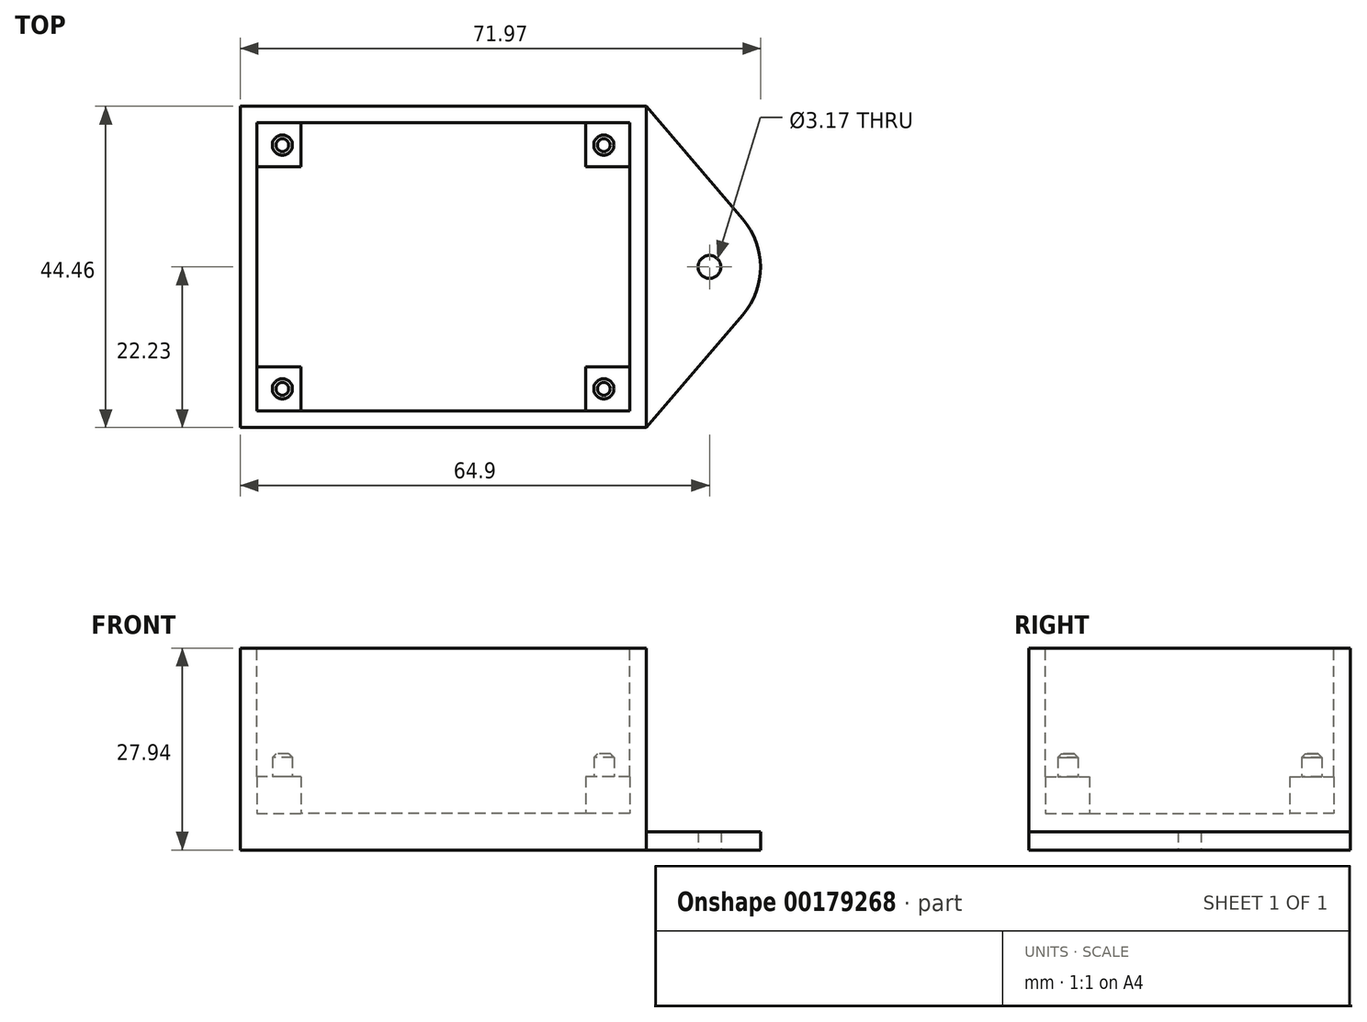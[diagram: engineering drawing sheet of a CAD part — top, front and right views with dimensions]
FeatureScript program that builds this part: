
annotation { "Feature Type Name" : "Feature", "Feature Type Description" : "" }
export const myFeature = defineFeature(function(context is Context, id is Id, definition is map)
    precondition{}
    {
        {
            var Q0;
            Q0=qCreatedBy(makeId("Top.planeOp"),FACE);
            var sketch = newSketch(context, id + "F0", { "sketchPlane" : qUnion([Q0])});
            skLineSegment(sketch, "E0.bottom", {"start": v(28.07, -22.23) * mm, "end": v(-28.07, -22.23) * mm});
            skLineSegment(sketch, "E0.top", {"start": v(28.07, 22.23) * mm, "end": v(-28.07, 22.22) * mm});
            skLineSegment(sketch, "E0.left", {"start": v(28.07, -22.23) * mm, "end": v(28.07, 22.23) * mm});
            skLineSegment(sketch, "E0.right", {"start": v(-28.07, -22.23) * mm, "end": v(-28.07, 22.23) * mm});
            skPoint(sketch, "E0.middle", {"position": v(0, 0) * mm});
            skSolve(sketch);
        }
        {
            var Q0;
            Q0 = qSketchRegion(id + "F0", true);
            extrude(context, id + "F1", {"entities" : qUnion([Q0]), "depth" : 27.94 * mm});
        }
        {
            var Q0;
            Q0=makeQuery(id+"F1.opExtrude","CAP_FACE",FACE,{"disambiguationData":[OSD([sQuery(id+"F0.wireOp",EDGE,"E0.bottom"),sQuery(id+"F0.wireOp",EDGE,"E0.top"),sQuery(id+"F0.wireOp",EDGE,"E0.left"),sQuery(id+"F0.wireOp",EDGE,"E0.right")])],"isStart":false});
            var sketch = newSketch(context, id + "F2", { "sketchPlane" : qUnion([Q0])});
            skLineSegment(sketch, "E1.0", {"start": v(25.78, 19.94) * mm, "end": v(-25.78, 19.94) * mm});
            skLineSegment(sketch, "E1.1", {"start": v(25.78, -19.94) * mm, "end": v(25.78, 19.94) * mm});
            skLineSegment(sketch, "E1.2", {"start": v(25.78, -19.94) * mm, "end": v(-25.78, -19.94) * mm});
            skLineSegment(sketch, "E1.3", {"start": v(-25.78, -19.94) * mm, "end": v(-25.78, 19.94) * mm});
            skSolve(sketch);
        }
        {
            var Q0;
            Q0 = qSketchRegion(id + "F2", true);
            extrude(context, id + "F3", {"entities" : qUnion([Q0]), "operationType" : NewBodyOperationType.REMOVE, "oppositeDirection" : true, "depth" : 22.86 * mm});
        }
        {
            var Q0;
            Q0=makeQuery(id+"F3.boolean.opBoolean","COPY",FACE,{"derivedFrom":makeQuery(id+"F3.opExtrude","CAP_FACE",FACE,{"disambiguationData":[OSD([sQuery(id+"F2.wireOp",EDGE,"E1.0"),sQuery(id+"F2.wireOp",EDGE,"E1.1"),sQuery(id+"F2.wireOp",EDGE,"E1.2"),sQuery(id+"F2.wireOp",EDGE,"E1.3")])],"isStart":false})});
            var sketch = newSketch(context, id + "F4", { "sketchPlane" : qUnion([Q0])});
            skLineSegment(sketch, "E2.bottom", {"start": v(-25.78, 19.94) * mm, "end": v(-19.69, 19.94) * mm});
            skLineSegment(sketch, "E2.top", {"start": v(-25.78, 13.84) * mm, "end": v(-19.69, 13.84) * mm});
            skLineSegment(sketch, "E2.left", {"start": v(-25.78, 19.94) * mm, "end": v(-25.78, 13.84) * mm});
            skLineSegment(sketch, "E2.right", {"start": v(-19.69, 19.94) * mm, "end": v(-19.69, 13.84) * mm});
            skLineSegment(sketch, "E3.MirrorCS", {"start": v(25.78, 19.94) * mm, "end": v(25.78, 13.84) * mm});
            skLineSegment(sketch, "E4.MirrorCS", {"start": v(19.69, 19.94) * mm, "end": v(19.69, 13.84) * mm});
            skLineSegment(sketch, "E5.MirrorCS", {"start": v(25.78, 13.84) * mm, "end": v(19.69, 13.84) * mm});
            skLineSegment(sketch, "E6.MirrorCS", {"start": v(25.78, 19.94) * mm, "end": v(19.69, 19.94) * mm});
            skLineSegment(sketch, "E7.MirrorCS", {"start": v(-25.78, -13.84) * mm, "end": v(-19.69, -13.84) * mm});
            skLineSegment(sketch, "E8.MirrorCS", {"start": v(-25.78, -19.94) * mm, "end": v(-25.78, -13.84) * mm});
            skLineSegment(sketch, "E9.MirrorCS", {"start": v(-19.69, -19.94) * mm, "end": v(-19.69, -13.84) * mm});
            skLineSegment(sketch, "E10.MirrorCS", {"start": v(-25.78, -19.94) * mm, "end": v(-19.69, -19.94) * mm});
            skLineSegment(sketch, "E11.MirrorCS", {"start": v(25.78, -13.84) * mm, "end": v(19.69, -13.84) * mm});
            skLineSegment(sketch, "E12.MirrorCS", {"start": v(19.69, -19.94) * mm, "end": v(19.69, -13.84) * mm});
            skLineSegment(sketch, "E13.MirrorCS", {"start": v(25.78, -19.94) * mm, "end": v(25.78, -13.84) * mm});
            skLineSegment(sketch, "E14.MirrorCS", {"start": v(25.78, -19.94) * mm, "end": v(19.69, -19.94) * mm});
            skSolve(sketch);
        }
        {
            var Q0;
            Q0 = qSketchRegion(id + "F4", true);
            extrude(context, id + "F5", {"entities" : qUnion([Q0]), "operationType" : NewBodyOperationType.ADD, "depth" : 5.08 * mm});
        }
        {
            var Q0;
            Q0=makeQuery(id+"F5.opExtrude","CAP_FACE",FACE,{"disambiguationData":[OSD([sQuery(id+"F4.wireOp",EDGE,"E2.bottom"),sQuery(id+"F4.wireOp",EDGE,"E2.top"),sQuery(id+"F4.wireOp",EDGE,"E2.left"),sQuery(id+"F4.wireOp",EDGE,"E2.right")])],"isStart":false});
            var sketch = newSketch(context, id + "F6", { "sketchPlane" : qUnion([Q0])});
            skLineSegment(sketch, "E15.bottom", {"start": v(22.23, -16.86) * mm, "end": v(-22.23, -16.86) * mm, "construction": true});
            skLineSegment(sketch, "E15.top", {"start": v(22.23, 16.86) * mm, "end": v(-22.23, 16.86) * mm, "construction": true});
            skLineSegment(sketch, "E15.left", {"start": v(22.23, -16.86) * mm, "end": v(22.23, 16.86) * mm, "construction": true});
            skLineSegment(sketch, "E15.right", {"start": v(-22.23, -16.86) * mm, "end": v(-22.23, 16.86) * mm, "construction": true});
            skPoint(sketch, "E15.middle", {"position": v(0, 0) * mm});
            skCircle(sketch, "E16", {"center": v(-22.23, 16.86) * mm, "radius": 1.4 * mm});
            skCircle(sketch, "E17.MirrorC", {"center": v(22.23, 16.86) * mm, "radius": 1.4 * mm});
            skCircle(sketch, "E18.MirrorC", {"center": v(22.23, -16.86) * mm, "radius": 1.4 * mm});
            skCircle(sketch, "E19.MirrorC", {"center": v(-22.23, -16.86) * mm, "radius": 1.4 * mm});
            skSolve(sketch);
        }
        {
            var Q0;
            Q0 = qSketchRegion(id + "F6", true);
            extrude(context, id + "F7", {"entities" : qUnion([Q0]), "operationType" : NewBodyOperationType.ADD, "depth" : 3.17 * mm});
        }
        {
            var Q0;
            Q0=makeQuery(id+"F7.opExtrude","CAP_EDGE",EDGE,{"disambiguationData":[OSD([sQuery(id+"F6.wireOp",EDGE,"E16")])],"isStart":false});
            var Q1;
            Q1=makeQuery(id+"F7.opExtrude","CAP_EDGE",EDGE,{"disambiguationData":[OSD([sQuery(id+"F6.wireOp",EDGE,"E17.MirrorC")])],"isStart":false});
            var Q2;
            Q2=makeQuery(id+"F7.opExtrude","CAP_EDGE",EDGE,{"disambiguationData":[OSD([sQuery(id+"F6.wireOp",EDGE,"E19.MirrorC")])],"isStart":false});
            var Q3;
            Q3=makeQuery(id+"F7.opExtrude","CAP_EDGE",EDGE,{"disambiguationData":[OSD([sQuery(id+"F6.wireOp",EDGE,"E18.MirrorC")])],"isStart":false});
            chamfer(context, id + "F8", {"entities" : qUnion([Q0, Q1, Q2, Q3]), "width" : 0.5 * mm, "tangentPropagation" : true});
        }
        {
            var Q0;
            Q0=makeQuery(id+"F1.opExtrude","CAP_FACE",FACE,{"disambiguationData":[OSD([sQuery(id+"F0.wireOp",EDGE,"E0.bottom"),sQuery(id+"F0.wireOp",EDGE,"E0.top"),sQuery(id+"F0.wireOp",EDGE,"E0.left"),sQuery(id+"F0.wireOp",EDGE,"E0.right")])],"isStart":true});
            var sketch = newSketch(context, id + "F9", { "sketchPlane" : qUnion([Q0])});
            skLineSegment(sketch, "E20", {"start": v(28.07, 22.23) * mm, "end": v(41.45, 6.61) * mm});
            skLineSegment(sketch, "E21", {"start": v(41.45, -6.61) * mm, "end": v(28.07, -22.23) * mm});
            skPoint(sketch, "E22.visualSharp", {"position": v(47.12, 0) * mm});
            skArc(sketch, "E22.filletArc", {"start": v(41.45, -6.61) * mm, "mid": v(43.9, 0) * mm, "end": v(41.45, 6.61) * mm});
            skLineSegment(sketch, "E23", {"start": v(28.07, 22.23) * mm, "end": v(28.07, -22.23) * mm});
            skArc(sketch, "E24.MirrorCS", {"start": v(-41.45, -6.61) * mm, "mid": v(-43.9, 0) * mm, "end": v(-41.45, 6.61) * mm});
            skLineSegment(sketch, "E25.MirrorCS", {"start": v(-41.45, -6.61) * mm, "end": v(-28.07, -22.23) * mm});
            skLineSegment(sketch, "E26.MirrorCS", {"start": v(-28.07, 22.23) * mm, "end": v(-41.45, 6.61) * mm});
            skLineSegment(sketch, "E27.MirrorCS", {"start": v(-28.07, 22.23) * mm, "end": v(-28.07, -22.23) * mm});
            skPoint(sketch, "E28.MirrorP", {"position": v(-47.12, 0) * mm});
            skSolve(sketch);
        }
        {
            var Q0;
            Q0=makeQuery(id+"F9.imprint","IMPRINT",FACE,{"disambiguationData":[TD([[makeQuery(id+"F9.imprint","IMPRINT",EDGE,{"derivedFrom":sQuery(id+"F9.wireOp",EDGE,"E20")}),-1.0]])]});
            var Q1;
            Q1=makeQuery(id+"F9.imprint","IMPRINT",FACE,{"disambiguationData":[TD([[makeQuery(id+"F9.imprint","IMPRINT",EDGE,{"derivedFrom":sQuery(id+"F9.wireOp",EDGE,"E24.MirrorCS")}),-1.0]])]});
            extrude(context, id + "F10", {"entities" : qUnion([Q0, Q1]), "operationType" : NewBodyOperationType.ADD, "oppositeDirection" : true, "depth" : 2.54 * mm});
        }
        {
            var Q0;
            Q0=makeQuery(id+"F10.boolean.opBoolean","MERGE",FACE,{"derivedFrom":[makeQuery(id+"F1.opExtrude","CAP_FACE",FACE,{"disambiguationData":[OSD([sQuery(id+"F0.wireOp",EDGE,"E0.bottom"),sQuery(id+"F0.wireOp",EDGE,"E0.top"),sQuery(id+"F0.wireOp",EDGE,"E0.left"),sQuery(id+"F0.wireOp",EDGE,"E0.right")])],"isStart":true}),makeQuery(id+"F10.opExtrude","CAP_FACE",FACE,{"disambiguationData":[OSD([sQuery(id+"F9.wireOp",EDGE,"E20"),sQuery(id+"F9.wireOp",EDGE,"E21"),sQuery(id+"F9.wireOp",EDGE,"E22.filletArc"),sQuery(id+"F9.wireOp",EDGE,"E23")])],"isStart":true}),makeQuery(id+"F10.opExtrude","CAP_FACE",FACE,{"disambiguationData":[OSD([sQuery(id+"F9.wireOp",EDGE,"E24.MirrorCS"),sQuery(id+"F9.wireOp",EDGE,"E25.MirrorCS"),sQuery(id+"F9.wireOp",EDGE,"E26.MirrorCS"),sQuery(id+"F9.wireOp",EDGE,"E27.MirrorCS")])],"isStart":true})]});
            var sketch = newSketch(context, id + "F11", { "sketchPlane" : qUnion([Q0])});
            skCircle(sketch, "E29", {"center": v(36.83, 0) * mm, "radius": 1.59 * mm});
            skCircle(sketch, "E30.MirrorC", {"center": v(-36.83, 0) * mm, "radius": 1.59 * mm});
            skSolve(sketch);
        }
        {
            var Q0;
            Q0=makeQuery(id+"F11.imprint","IMPRINT",FACE,{"disambiguationData":[TD([[makeQuery(id+"F11.imprint","IMPRINT",EDGE,{"derivedFrom":sQuery(id+"F11.wireOp",EDGE,"E30.MirrorC")}),-1.0]])]});
            var Q1;
            Q1=makeQuery(id+"F11.imprint","IMPRINT",FACE,{"disambiguationData":[TD([[makeQuery(id+"F11.imprint","IMPRINT",EDGE,{"derivedFrom":sQuery(id+"F11.wireOp",EDGE,"E29")}),1.0]])]});
            extrude(context, id + "F12", {"entities" : qUnion([Q0, Q1]), "operationType" : NewBodyOperationType.REMOVE, "oppositeDirection" : true, "depth" : 25.4 * mm});
        }
    });
